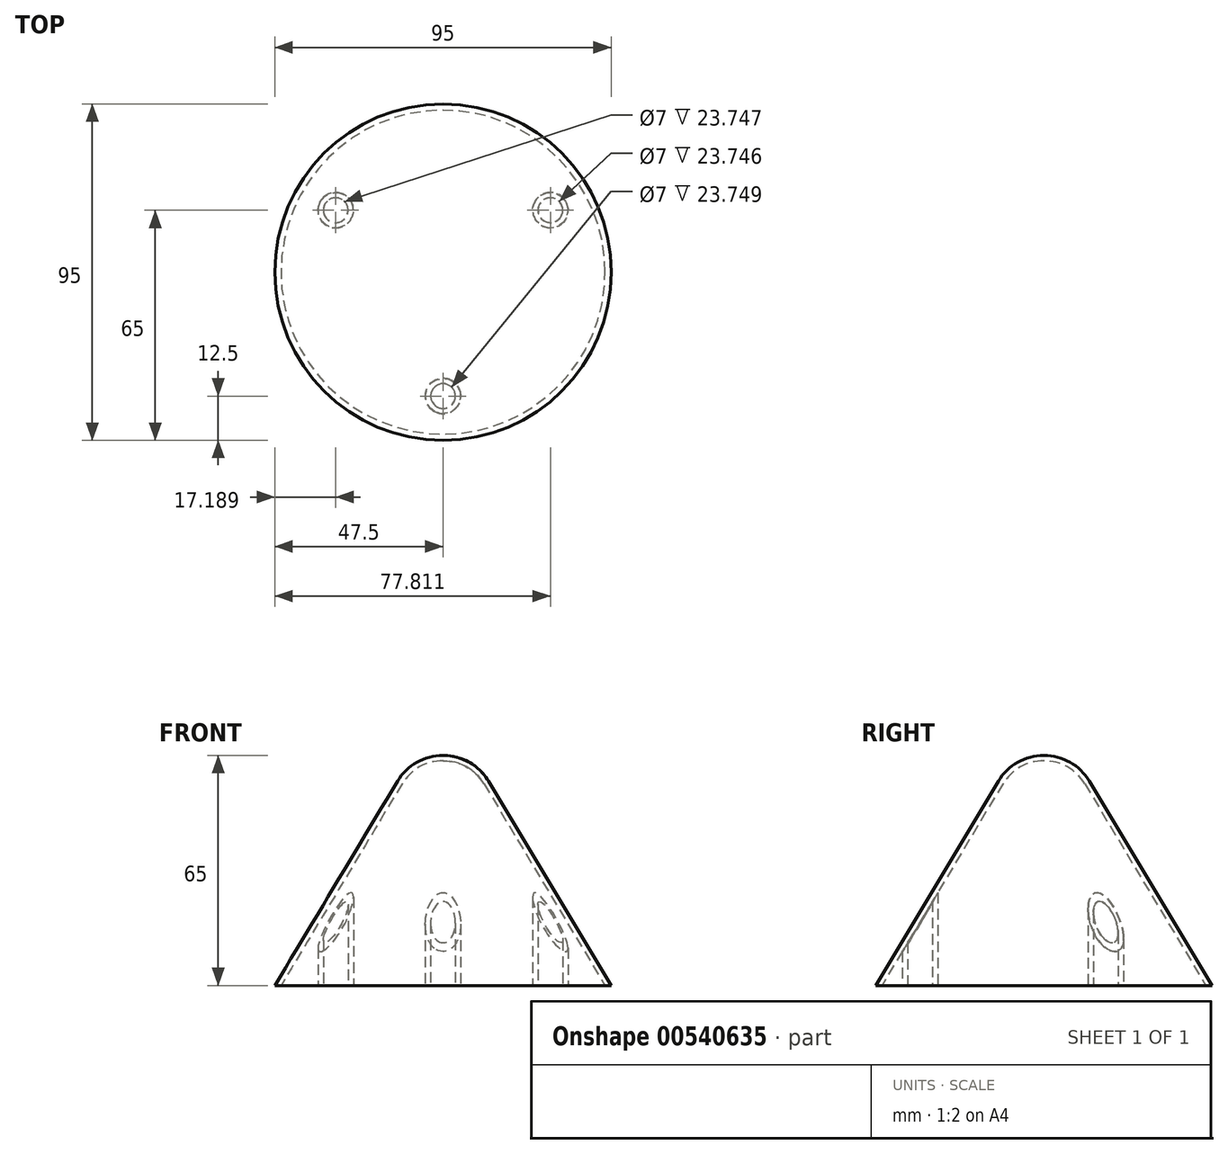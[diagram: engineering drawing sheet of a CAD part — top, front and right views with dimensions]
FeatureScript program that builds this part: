
annotation { "Feature Type Name" : "Feature", "Feature Type Description" : "" }
export const myFeature = defineFeature(function(context is Context, id is Id, definition is map)
    precondition{}
    {
        {
            var Q0;
            Q0=qCreatedBy(makeId("Front.planeOp"),FACE);
            var sketch = newSketch(context, id + "F0", { "sketchPlane" : qUnion([Q0])});
            skLineSegment(sketch, "E0", {"start": v(0, 0) * mm, "end": v(47.5, 0) * mm});
            skLineSegment(sketch, "E1", {"start": v(0, 0) * mm, "end": v(0, 50) * mm});
            skArc(sketch, "E2", {"start": v(12.86, 57.72) * mm, "mid": v(7.39, 63.05) * mm, "end": v(0, 65) * mm});
            skLineSegment(sketch, "E3", {"start": v(12.86, 57.72) * mm, "end": v(47.5, 0) * mm});
            skLineSegment(sketch, "E4", {"start": v(0, 50) * mm, "end": v(0, 65) * mm});
            skPoint(sketch, "E4.endSnap0", {"position": v(0, 65) * mm});
            skPoint(sketch, "E5.orphan", {"position": v(-12.86, 57.72) * mm});
            skPoint(sketch, "E6.orphan", {"position": v(0, 83.48) * mm});
            skSolve(sketch);
        }
        {
            var Q0;
            Q0=makeQuery(id+"F0.imprint","IMPRINT",FACE,{"disambiguationData":[TD([[makeQuery(id+"F0.imprint","IMPRINT",EDGE,{"derivedFrom":sQuery(id+"F0.wireOp",EDGE,"E0")}),1.0]])]});
            var Q1;
            Q1=sQuery(id+"F0.wireOp",EDGE,"E1");
            revolve(context, id + "F1", {"entities" : qUnion([Q0]), "axis" : qUnion([Q1]), "revolveType" : RevolveType.FULL});
        }
        {
            var Q0;
            Q0=makeQuery(id+"F1.opRevolve","SWEPT_FACE",FACE,{"disambiguationData":[OSD([sQuery(id+"F0.wireOp",EDGE,"E0")])]});
            shell(context, id + "F2", {"entities" : qUnion([Q0]), "thickness" : 1.5 * mm});
        }
        {
            var Q0;
            Q0=qCreatedBy(makeId("Top.planeOp"),FACE);
            var sketch = newSketch(context, id + "F3", { "sketchPlane" : qUnion([Q0])});
            skCircle(sketch, "E7", {"center": v(0, -35) * mm, "radius": 5 * mm});
            skCircle(sketch, "E8.1.0", {"center": v(30.31, 17.5) * mm, "radius": 5 * mm});
            skCircle(sketch, "E8.2.0", {"center": v(-30.31, 17.5) * mm, "radius": 5 * mm});
            skPoint(sketch, "E8.center", {"position": v(0, 0) * mm});
            skSolve(sketch);
        }
        {
            var Q0;
            Q0 = qSketchRegion(id + "F3", true);
            extrude(context, id + "F4", {"entities" : qUnion([Q0]), "operationType" : NewBodyOperationType.ADD, "endBound" : BoundingType.UP_TO_NEXT, "depth" : 25 * mm, "offsetDistance" : 25 * mm});
        }
        {
            var Q0;
            Q0=makeQuery(id+"F4.opExtrude","CAP_FACE",FACE,{"disambiguationData":[OSD([sQuery(id+"F3.wireOp",EDGE,"E8.1.0")])],"isStart":true});
            var Q1;
            Q1=makeQuery(id+"F4.opExtrude","CAP_FACE",FACE,{"disambiguationData":[OSD([sQuery(id+"F3.wireOp",EDGE,"E7")])],"isStart":true});
            var Q2;
            Q2=makeQuery(id+"F4.opExtrude","CAP_FACE",FACE,{"disambiguationData":[OSD([sQuery(id+"F3.wireOp",EDGE,"E8.2.0")])],"isStart":true});
            shell(context, id + "F5", {"entities" : qUnion([Q0, Q1, Q2]), "thickness" : 1.5 * mm});
        }
    });
